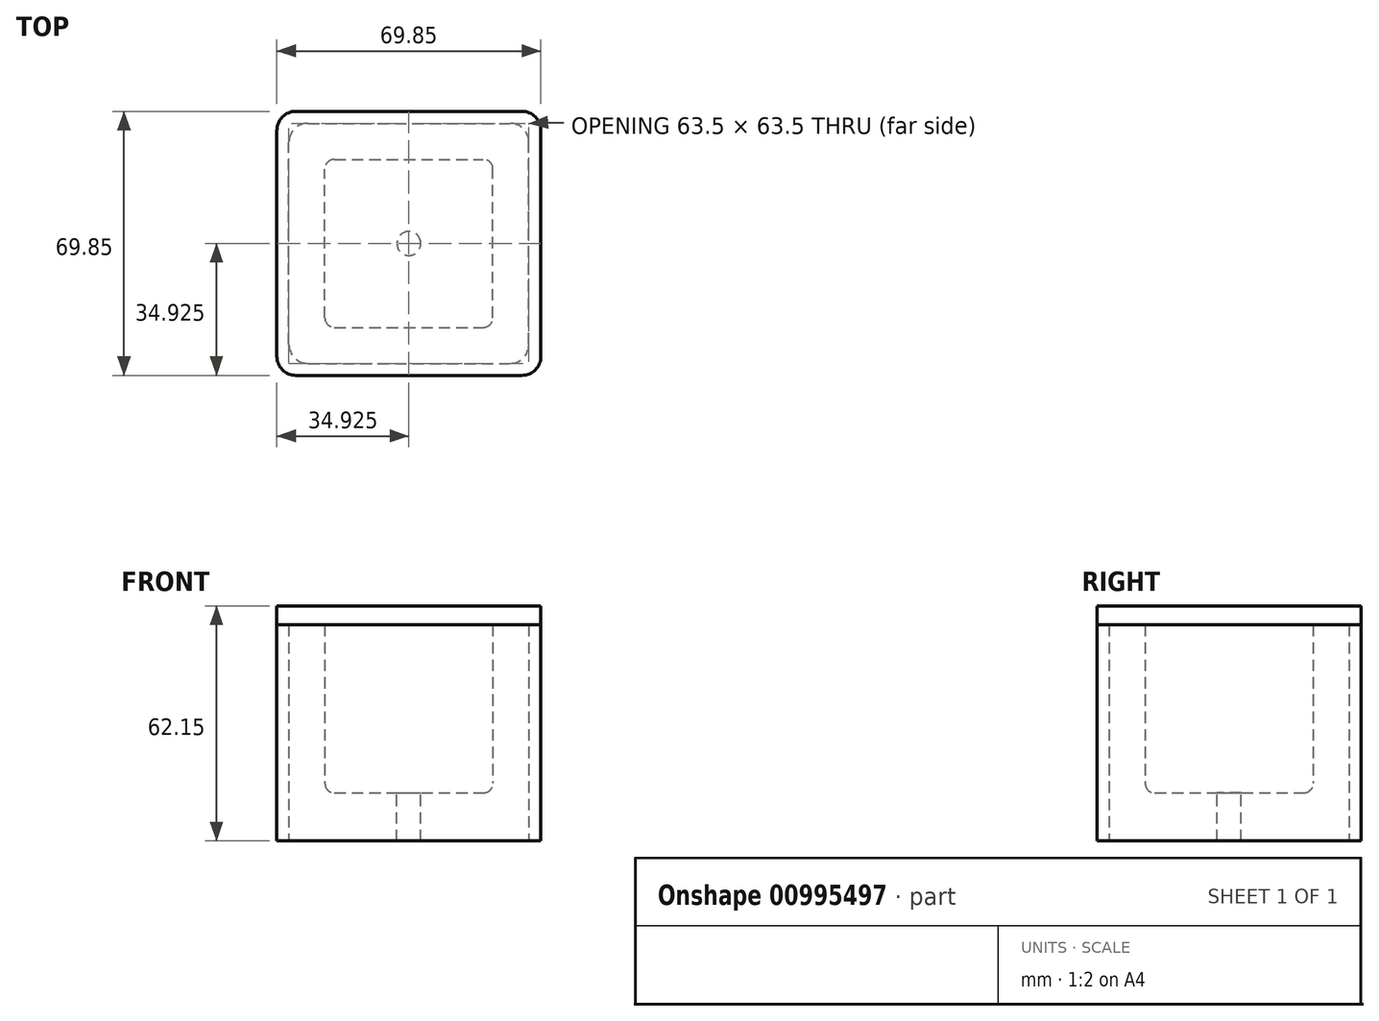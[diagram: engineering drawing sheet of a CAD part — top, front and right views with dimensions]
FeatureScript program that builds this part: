
annotation { "Feature Type Name" : "Feature", "Feature Type Description" : "" }
export const myFeature = defineFeature(function(context is Context, id is Id, definition is map)
    precondition{}
    {
        {
            var Q0;
            Q0=qCreatedBy(makeId("Top.planeOp"),FACE);
            var sketch = newSketch(context, id + "F0", { "sketchPlane" : qUnion([Q0])});
            skLineSegment(sketch, "E0.bottom", {"start": v(0, 0) * mm, "end": v(44.45, 0) * mm});
            skLineSegment(sketch, "E0.top", {"start": v(0, 44.45) * mm, "end": v(44.45, 44.45) * mm});
            skLineSegment(sketch, "E0.left", {"start": v(0, 0) * mm, "end": v(0, 44.45) * mm});
            skLineSegment(sketch, "E0.right", {"start": v(44.45, 0) * mm, "end": v(44.45, 44.45) * mm});
            skLineSegment(sketch, "E1.bottom", {"start": v(-9.52, -9.53) * mm, "end": v(53.98, -9.53) * mm});
            skLineSegment(sketch, "E1.top", {"start": v(-9.53, 53.98) * mm, "end": v(53.97, 53.98) * mm});
            skLineSegment(sketch, "E1.left", {"start": v(-9.52, -9.52) * mm, "end": v(-9.53, 53.98) * mm});
            skLineSegment(sketch, "E1.right", {"start": v(53.98, -9.52) * mm, "end": v(53.97, 53.98) * mm});
            skLineSegment(sketch, "E2.bottom", {"start": v(-12.7, -12.7) * mm, "end": v(57.15, -12.7) * mm});
            skLineSegment(sketch, "E2.top", {"start": v(-12.7, 57.15) * mm, "end": v(57.15, 57.15) * mm});
            skLineSegment(sketch, "E2.left", {"start": v(-12.7, -12.7) * mm, "end": v(-12.7, 57.15) * mm});
            skLineSegment(sketch, "E2.right", {"start": v(57.15, -12.7) * mm, "end": v(57.15, 57.15) * mm});
            skSolve(sketch);
        }
        {
            var Q0;
            Q0=makeQuery(id+"F0.imprint","IMPRINT",FACE,{"disambiguationData":[TD([[makeQuery(id+"F0.imprint","IMPRINT",EDGE,{"derivedFrom":sQuery(id+"F0.wireOp",EDGE,"E1.bottom")}),-1.0]])]});
            var Q1;
            Q1=makeQuery(id+"F0.imprint","IMPRINT",FACE,{"disambiguationData":[TD([[makeQuery(id+"F0.imprint","IMPRINT",EDGE,{"derivedFrom":sQuery(id+"F0.wireOp",EDGE,"E0.bottom")}),1.0]])]});
            extrude(context, id + "F1", {"entities" : qUnion([Q0, Q1]), "depth" : 44.45 * mm, "offsetDistance" : 25.4 * mm});
        }
        {
            var Q0;
            Q0=makeQuery(id+"F1.opExtrude","CAP_FACE",FACE,{"disambiguationData":[OSD([sQuery(id+"F0.wireOp",EDGE,"E1.bottom"),sQuery(id+"F0.wireOp",EDGE,"E1.top"),sQuery(id+"F0.wireOp",EDGE,"E1.left"),sQuery(id+"F0.wireOp",EDGE,"E1.right"),sQuery(id+"F0.wireOp",EDGE,"E2.bottom"),sQuery(id+"F0.wireOp",EDGE,"E2.top"),sQuery(id+"F0.wireOp",EDGE,"E2.left"),sQuery(id+"F0.wireOp",EDGE,"E2.right")])],"isStart":false});
            var sketch = newSketch(context, id + "F2", { "sketchPlane" : qUnion([Q0])});
            skLineSegment(sketch, "E3.bottom", {"start": v(-12.7, 57.15) * mm, "end": v(57.15, 57.15) * mm});
            skLineSegment(sketch, "E3.top", {"start": v(-12.7, -12.7) * mm, "end": v(57.15, -12.7) * mm});
            skLineSegment(sketch, "E3.left", {"start": v(-12.7, 57.15) * mm, "end": v(-12.7, -12.7) * mm});
            skLineSegment(sketch, "E3.right", {"start": v(57.15, 57.15) * mm, "end": v(57.15, -12.7) * mm});
            skSolve(sketch);
        }
        {
            var Q0;
            Q0 = qSketchRegion(id + "F2", true);
            extrude(context, id + "F3", {"entities" : qUnion([Q0]), "depth" : 5 * mm, "offsetDistance" : 25.4 * mm});
        }
        {
            var Q0;
            Q0=makeQuery(id+"F1.opExtrude","CAP_FACE",FACE,{"disambiguationData":[OSD([sQuery(id+"F0.wireOp",EDGE,"E1.bottom"),sQuery(id+"F0.wireOp",EDGE,"E1.top"),sQuery(id+"F0.wireOp",EDGE,"E1.left"),sQuery(id+"F0.wireOp",EDGE,"E1.right"),sQuery(id+"F0.wireOp",EDGE,"E2.bottom"),sQuery(id+"F0.wireOp",EDGE,"E2.top"),sQuery(id+"F0.wireOp",EDGE,"E2.left"),sQuery(id+"F0.wireOp",EDGE,"E2.right")])],"isStart":true});
            var sketch = newSketch(context, id + "F4", { "sketchPlane" : qUnion([Q0])});
            skLineSegment(sketch, "E4.bottom", {"start": v(-12.7, 12.7) * mm, "end": v(57.15, 12.7) * mm});
            skLineSegment(sketch, "E4.top", {"start": v(-12.7, -57.15) * mm, "end": v(57.15, -57.15) * mm});
            skLineSegment(sketch, "E4.left", {"start": v(-12.7, 12.7) * mm, "end": v(-12.7, -57.15) * mm});
            skLineSegment(sketch, "E4.right", {"start": v(57.15, 12.7) * mm, "end": v(57.15, -57.15) * mm});
            skLineSegment(sketch, "E5.bottom", {"start": v(53.97, -53.98) * mm, "end": v(-9.53, -53.98) * mm});
            skLineSegment(sketch, "E5.top", {"start": v(53.97, 9.53) * mm, "end": v(-9.53, 9.53) * mm});
            skLineSegment(sketch, "E5.left", {"start": v(53.97, -53.98) * mm, "end": v(53.97, 9.52) * mm});
            skLineSegment(sketch, "E5.right", {"start": v(-9.52, -53.98) * mm, "end": v(-9.52, 9.52) * mm});
            skSolve(sketch);
        }
        {
            var Q0;
            Q0 = qSketchRegion(id + "F4", true);
            extrude(context, id + "F5", {"entities" : qUnion([Q0]), "operationType" : NewBodyOperationType.ADD, "depth" : 12.7 * mm, "offsetDistance" : 25.4 * mm});
        }
        {
            var Q0;
            Q0=makeQuery(id+"F5.boolean.opBoolean","MERGE",EDGE,{"derivedFrom":[makeQuery(id+"F1.opExtrude","SWEPT_EDGE",EDGE,{"disambiguationData":[OSD([sQuery(id+"F0.wireOp",EDGE,"E1.bottom"),sQuery(id+"F0.wireOp",EDGE,"E1.right")])]}),makeQuery(id+"F5.opExtrude","SWEPT_EDGE",EDGE,{"disambiguationData":[OSD([sQuery(id+"F4.wireOp",EDGE,"E5.top"),sQuery(id+"F4.wireOp",EDGE,"E5.left")])]})]});
            var Q1;
            Q1=makeQuery(id+"F5.boolean.opBoolean","MERGE",EDGE,{"derivedFrom":[makeQuery(id+"F1.opExtrude","SWEPT_EDGE",EDGE,{"disambiguationData":[OSD([sQuery(id+"F0.wireOp",EDGE,"E1.bottom"),sQuery(id+"F0.wireOp",EDGE,"E1.left")])]}),makeQuery(id+"F5.opExtrude","SWEPT_EDGE",EDGE,{"disambiguationData":[OSD([sQuery(id+"F4.wireOp",EDGE,"E5.top"),sQuery(id+"F4.wireOp",EDGE,"E5.right")])]})]});
            var Q2;
            Q2=makeQuery(id+"F5.boolean.opBoolean","MERGE",EDGE,{"derivedFrom":[makeQuery(id+"F1.opExtrude","SWEPT_EDGE",EDGE,{"disambiguationData":[OSD([sQuery(id+"F0.wireOp",EDGE,"E1.top"),sQuery(id+"F0.wireOp",EDGE,"E1.left")])]}),makeQuery(id+"F5.opExtrude","SWEPT_EDGE",EDGE,{"disambiguationData":[OSD([sQuery(id+"F4.wireOp",EDGE,"E5.bottom"),sQuery(id+"F4.wireOp",EDGE,"E5.right")])]})]});
            var Q3;
            Q3=makeQuery(id+"F5.boolean.opBoolean","MERGE",EDGE,{"derivedFrom":[makeQuery(id+"F1.opExtrude","SWEPT_EDGE",EDGE,{"disambiguationData":[OSD([sQuery(id+"F0.wireOp",EDGE,"E1.top"),sQuery(id+"F0.wireOp",EDGE,"E1.right")])]}),makeQuery(id+"F5.opExtrude","SWEPT_EDGE",EDGE,{"disambiguationData":[OSD([sQuery(id+"F4.wireOp",EDGE,"E5.bottom"),sQuery(id+"F4.wireOp",EDGE,"E5.left")])]})]});
            var Q4;
            Q4=makeQuery(id+"F5.boolean.opBoolean","MERGE",EDGE,{"derivedFrom":[makeQuery(id+"F1.opExtrude","SWEPT_EDGE",EDGE,{"disambiguationData":[OSD([sQuery(id+"F0.wireOp",EDGE,"E2.bottom"),sQuery(id+"F0.wireOp",EDGE,"E2.left")])]}),makeQuery(id+"F5.opExtrude","SWEPT_EDGE",EDGE,{"disambiguationData":[OSD([sQuery(id+"F4.wireOp",EDGE,"E4.bottom"),sQuery(id+"F4.wireOp",EDGE,"E4.left")])]})]});
            var Q5;
            Q5=makeQuery(id+"F5.boolean.opBoolean","MERGE",EDGE,{"derivedFrom":[makeQuery(id+"F1.opExtrude","SWEPT_EDGE",EDGE,{"disambiguationData":[OSD([sQuery(id+"F0.wireOp",EDGE,"E2.top"),sQuery(id+"F0.wireOp",EDGE,"E2.left")])]}),makeQuery(id+"F5.opExtrude","SWEPT_EDGE",EDGE,{"disambiguationData":[OSD([sQuery(id+"F4.wireOp",EDGE,"E4.top"),sQuery(id+"F4.wireOp",EDGE,"E4.left")])]})]});
            var Q6;
            Q6=makeQuery(id+"F5.boolean.opBoolean","MERGE",EDGE,{"derivedFrom":[makeQuery(id+"F1.opExtrude","SWEPT_EDGE",EDGE,{"disambiguationData":[OSD([sQuery(id+"F0.wireOp",EDGE,"E2.top"),sQuery(id+"F0.wireOp",EDGE,"E2.right")])]}),makeQuery(id+"F5.opExtrude","SWEPT_EDGE",EDGE,{"disambiguationData":[OSD([sQuery(id+"F4.wireOp",EDGE,"E4.top"),sQuery(id+"F4.wireOp",EDGE,"E4.right")])]})]});
            var Q7;
            Q7=makeQuery(id+"F5.boolean.opBoolean","MERGE",EDGE,{"derivedFrom":[makeQuery(id+"F1.opExtrude","SWEPT_EDGE",EDGE,{"disambiguationData":[OSD([sQuery(id+"F0.wireOp",EDGE,"E2.bottom"),sQuery(id+"F0.wireOp",EDGE,"E2.right")])]}),makeQuery(id+"F5.opExtrude","SWEPT_EDGE",EDGE,{"disambiguationData":[OSD([sQuery(id+"F4.wireOp",EDGE,"E4.bottom"),sQuery(id+"F4.wireOp",EDGE,"E4.right")])]})]});
            var Q8;
            Q8=makeQuery(id+"F3.opExtrude","SWEPT_EDGE",EDGE,{"disambiguationData":[OSD([sQuery(id+"F2.wireOp",EDGE,"E3.top"),sQuery(id+"F2.wireOp",EDGE,"E3.left")])]});
            fillet(context, id + "F6", {"entities" : qUnion([Q0, Q1, Q2, Q3, Q4, Q5, Q6, Q7, Q8]), "radius" : 5.08 * mm, "tangentPropagation" : true, "allowEdgeOverflow" : false});
        }
        {
            var Q0;
            Q0=makeQuery(id+"F1.opExtrude","SWEPT_EDGE",EDGE,{"disambiguationData":[OSD([sQuery(id+"F0.wireOp",EDGE,"E0.bottom"),sQuery(id+"F0.wireOp",EDGE,"E0.left")])]});
            var Q1;
            Q1=makeQuery(id+"F1.opExtrude","SWEPT_EDGE",EDGE,{"disambiguationData":[OSD([sQuery(id+"F0.wireOp",EDGE,"E0.bottom"),sQuery(id+"F0.wireOp",EDGE,"E0.right")])]});
            var Q2;
            Q2=makeQuery(id+"F1.opExtrude","SWEPT_EDGE",EDGE,{"disambiguationData":[OSD([sQuery(id+"F0.wireOp",EDGE,"E0.top"),sQuery(id+"F0.wireOp",EDGE,"E0.left")])]});
            var Q3;
            Q3=makeQuery(id+"F1.opExtrude","SWEPT_EDGE",EDGE,{"disambiguationData":[OSD([sQuery(id+"F0.wireOp",EDGE,"E0.top"),sQuery(id+"F0.wireOp",EDGE,"E0.right")])]});
            var Q4;
            Q4=makeQuery(id+"F1.opExtrude","CAP_EDGE",EDGE,{"disambiguationData":[OSD([sQuery(id+"F0.wireOp",EDGE,"E0.right")])],"isStart":true});
            var Q5;
            Q5=makeQuery(id+"F1.opExtrude","CAP_EDGE",EDGE,{"disambiguationData":[OSD([sQuery(id+"F0.wireOp",EDGE,"E0.top")])],"isStart":true});
            var Q6;
            Q6=makeQuery(id+"F1.opExtrude","CAP_EDGE",EDGE,{"disambiguationData":[OSD([sQuery(id+"F0.wireOp",EDGE,"E0.bottom")])],"isStart":true});
            var Q7;
            Q7=makeQuery(id+"F1.opExtrude","CAP_EDGE",EDGE,{"disambiguationData":[OSD([sQuery(id+"F0.wireOp",EDGE,"E0.left")])],"isStart":true});
            fillet(context, id + "F7", {"entities" : qUnion([Q0, Q1, Q2, Q3, Q4, Q5, Q6, Q7]), "radius" : 2.54 * mm, "tangentPropagation" : true, "allowEdgeOverflow" : false});
        }
        {
            var Q0;
            Q0=makeQuery(id+"F3.opExtrude","SWEPT_EDGE",EDGE,{"disambiguationData":[OSD([sQuery(id+"F2.wireOp",EDGE,"E3.bottom"),sQuery(id+"F2.wireOp",EDGE,"E3.right")])]});
            var Q1;
            Q1=makeQuery(id+"F3.opExtrude","SWEPT_EDGE",EDGE,{"disambiguationData":[OSD([sQuery(id+"F2.wireOp",EDGE,"E3.bottom"),sQuery(id+"F2.wireOp",EDGE,"E3.left")])]});
            var Q2;
            Q2=makeQuery(id+"F3.opExtrude","SWEPT_EDGE",EDGE,{"disambiguationData":[OSD([sQuery(id+"F2.wireOp",EDGE,"E3.top"),sQuery(id+"F2.wireOp",EDGE,"E3.right")])]});
            fillet(context, id + "F8", {"entities" : qUnion([Q0, Q1, Q2]), "radius" : 5.08 * mm, "tangentPropagation" : true, "allowEdgeOverflow" : false});
        }
        {
            var Q0;
            Q0=makeQuery(id+"F1.opExtrude","CAP_FACE",FACE,{"disambiguationData":[OSD([sQuery(id+"F0.wireOp",EDGE,"E0.bottom"),sQuery(id+"F0.wireOp",EDGE,"E0.top"),sQuery(id+"F0.wireOp",EDGE,"E0.left"),sQuery(id+"F0.wireOp",EDGE,"E0.right")])],"isStart":true});
            var sketch = newSketch(context, id + "F9", { "sketchPlane" : qUnion([Q0])});
            skLineSegment(sketch, "E6", {"start": v(2.54, -2.54) * mm, "end": v(41.9, -41.91) * mm, "construction": true});
            skLineSegment(sketch, "E7", {"start": v(41.9, -2.54) * mm, "end": v(2.54, -41.9) * mm, "construction": true});
            skCircle(sketch, "E8", {"center": v(22.23, -22.23) * mm, "radius": 3.18 * mm});
            skSolve(sketch);
        }
        {
            var Q0;
            Q0 = qSketchRegion(id + "F9", true);
            extrude(context, id + "F10", {"entities" : qUnion([Q0]), "operationType" : NewBodyOperationType.ADD, "depth" : 12.7 * mm, "offsetDistance" : 25.4 * mm});
        }
    });
